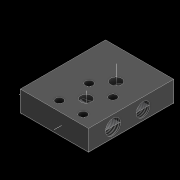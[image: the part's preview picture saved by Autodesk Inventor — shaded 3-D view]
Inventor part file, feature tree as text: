
AUTODESK INVENTOR PART (.ipt)
format: ipt  version: 2021 (Build 250183000, 183)  size: 283,136 bytes
history: native  units: in
note: dims shown in document units (in); Inventor stores cm internally (conversion verified against a paired STEP export)
features: other x12, direct_edit x5, hole x5, plane x4, move_body x4, sketch x3, extrude x2, thread x2, reference x2, mirror x1
ambient origin geometry x8: Origin, YZ Plane, XZ Plane, XY Plane, X Axis, Y Axis, Z Axis, Center Point
bodies: Solid1 (feature_tree)
feature tree (40):
  direct_edit  "Direct Edit1"
  plane  "Work Plane1"
  other  "Work Axis2"
  plane  "Work Plane2"
  extrude  "Extrusion1"  Depth=0.0591in TaperAngle=0.0deg
  plane  "Work Plane3"
  hole  "Hole2"  [1 undecoded]
  extrude  "Extrusion3"  Depth=1.9685in TaperAngle=0.0deg
  sketch  "Sketch4"  dims[d6=0.6184in d7=90.0deg d8=0.0in d9=0.0in d10=0.6299in]
  hole  "Hole6"  [1 undecoded]
  hole  "Hole7"  [1 undecoded]
  hole  "Hole10"  [1 undecoded]
  hole  "Hole12"  [1 undecoded]
  direct_edit  "Direct Edit4"
  direct_edit  "Direct Edit5"
  direct_edit  "Direct Edit6"
  direct_edit  "Direct Edit7"
  thread  "Thread1"  [1 undecoded]
  thread  "Thread3"  [1 undecoded]
  plane  "Work Plane4"
  mirror  "Mirror1"
  other  "Work Axis1"
  sketch  "Sketch3"  dims[d0=0.0in d1=0.0in d2=0.0591in d3=0.0in d4=0.0in d5=0.0591in]
  other  "Work Axis3"
  sketch  "Sketch6"  dims[d11=0.0in d12=0.0in d13=0.3937in d14=1.9685in d15=0.0in d16=0.315in d17=0.315in d20=0.2362in d28=0.2756in d29=0.2362in d30=0.1575in d31=0.0787in d32=90.0deg d33=1.9685in d34=0.8108in d35=0.4724in d36=1.3189in d37=0.0in d62=0.2362in d63=0.2362in d64=0.1575in d65=0.0787in d66=90.0deg d67=1.5123in d68=0.8108in d69=0.3937in d70=0.2362in d71=0.1575in d72=0.0787in d73=90.0deg d74=0.1575in d75=0.0in d90=0.315in d91=0.2362in d92=0.1575in d93=0.0787in d94=90.0deg d95=1.4961in d96=0.8108in d105=0.4331in d106=0.2362in d107=0.1575in d108=0.0787in d109=90.0deg d110=0.9449in d111=0.0in d112=-0.0394in d113=0.2362in d114=-0.0197in d115=-0.0394in d116=0.3937in d117=0.0in d120=0.3937in d121=0.0in d122=1.5748in d118=0.5635in d119=0.0295in d123=0.0148in]
  reference  "Reference1"
  reference  "Reference2"
  other  "Cut-Extrude26"
  move_body  "Move1"
  move_body  "Move2"
  move_body  "Move3"
  move_body  "Move4"
  parser-record x1  (decoder bookkeeping rows leaked as tree rows — omitted from the tree; the rows remain in map.json)
  other  "BodyV4.iam"
  other  "rotarynozzle:1"
  other  "iner_sleeve:1"
  other  "Size2"
  other  "Size3"
  other  "Size4"
  other  "Size5"
note: 7 required parameter values undecoded (feature->parameter linkage not recoverable at this tier; creation-order binding heuristic only, values carry confidence <= 0.55)
note: 1 file-system path scrubbed to <path> (originals preserved in map.json)
